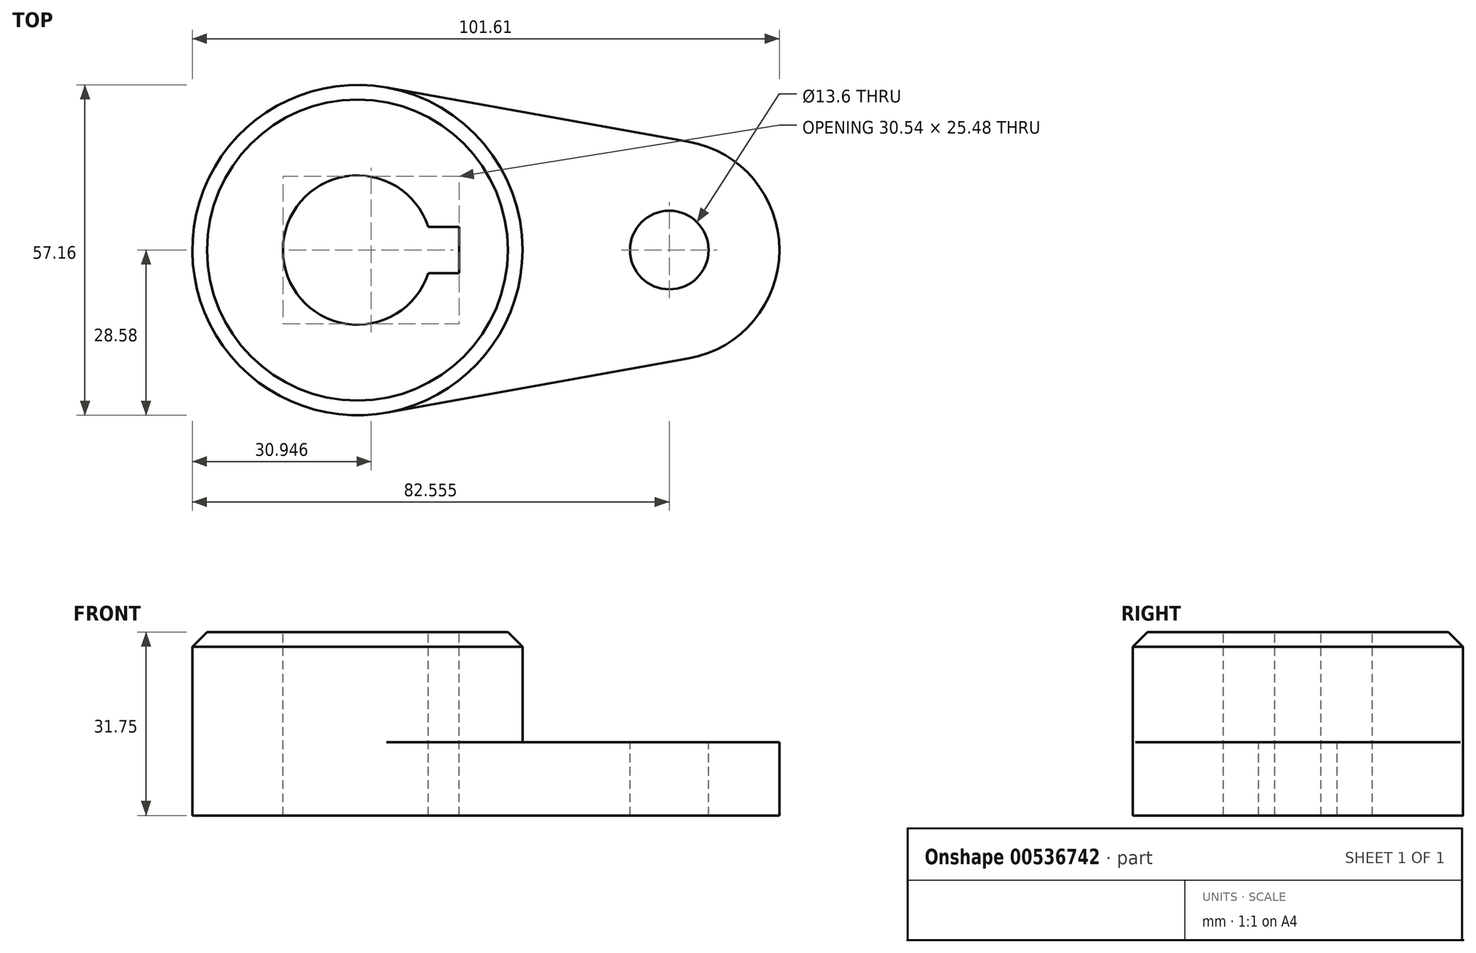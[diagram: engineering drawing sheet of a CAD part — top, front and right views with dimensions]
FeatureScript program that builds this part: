
annotation { "Feature Type Name" : "Feature", "Feature Type Description" : "" }
export const myFeature = defineFeature(function(context is Context, id is Id, definition is map)
    precondition{}
    {
        {
            var Q0;
            Q0=qCreatedBy(makeId("Top.planeOp"),FACE);
            var sketch = newSketch(context, id + "F0", { "sketchPlane" : qUnion([Q0])});
            skCircle(sketch, "E0", {"center": v(0, 0) * mm, "radius": 28.58 * mm});
            skArc(sketch, "E1", {"start": v(57.34, -18.75) * mm, "mid": v(73.03, 0) * mm, "end": v(57.34, 18.75) * mm});
            skLineSegment(sketch, "E2", {"start": v(57.34, 18.75) * mm, "end": v(5.04, 28.13) * mm});
            skLineSegment(sketch, "E3", {"start": v(5.04, -28.13) * mm, "end": v(57.34, -18.75) * mm});
            skSolve(sketch);
        }
        {
            var Q0;
            Q0 = qSketchRegion(id + "F0", true);
            extrude(context, id + "F1", {"entities" : qUnion([Q0]), "depth" : 12.7 * mm, "offsetDistance" : 25.4 * mm});
        }
        {
            var Q0;
            {var subQ0=sQuery(id+"F0.wireOp",EDGE,"E0");var subQ1=makeQuery(id+"F0.imprint","INTERSECT",VERTEX,{"derivedFrom":[subQ0,sQuery(id+"F0.wireOp",EDGE,"E2")]});Q0=makeQuery(id+"F0.imprint","IMPRINT",FACE,{"disambiguationData":[TD([[makeQuery(id+"F0.imprint","IMPRINT",EDGE,{"disambiguationData":[TD([[subQ1,-1.0]])],"derivedFrom":subQ0}),1.0]])]});}
            extrude(context, id + "F2", {"entities" : qUnion([Q0]), "operationType" : NewBodyOperationType.ADD, "depth" : 31.75 * mm, "offsetDistance" : 25.4 * mm});
        }
        {
            var Q0;
            Q0=makeQuery(id+"F1.opExtrude","CAP_FACE",FACE,{"disambiguationData":[OSD([sQuery(id+"F0.wireOp",EDGE,"E0"),sQuery(id+"F0.wireOp",EDGE,"E1"),sQuery(id+"F0.wireOp",EDGE,"E2"),sQuery(id+"F0.wireOp",EDGE,"E3")])],"isStart":false});
            var sketch = newSketch(context, id + "F3", { "sketchPlane" : qUnion([Q0])});
            skCircle(sketch, "E4", {"center": v(53.98, 0) * mm, "radius": 6.8 * mm});
            skSolve(sketch);
        }
        {
            var Q0;
            Q0 = qSketchRegion(id + "F3", true);
            extrude(context, id + "F4", {"entities" : qUnion([Q0]), "operationType" : NewBodyOperationType.REMOVE, "oppositeDirection" : true, "depth" : 25.4 * mm, "offsetDistance" : 25.4 * mm});
        }
        {
            var Q0;
            Q0=makeQuery(id+"F2.opExtrude","CAP_FACE",FACE,{"disambiguationData":[OSD([sQuery(id+"F0.wireOp",EDGE,"E0")])],"isStart":false});
            chamfer(context, id + "F5", {"entities" : qUnion([Q0]), "width" : 2.54 * mm, "tangentPropagation" : true});
        }
        {
            var Q0;
            Q0=makeQuery(id+"F2.opExtrude","CAP_FACE",FACE,{"disambiguationData":[OSD([sQuery(id+"F0.wireOp",EDGE,"E0")])],"isStart":false});
            var sketch = newSketch(context, id + "F6", { "sketchPlane" : qUnion([Q0])});
            skArc(sketch, "E5", {"start": v(12.26, 4.02) * mm, "mid": v(-12.9, 0) * mm, "end": v(12.26, -4.02) * mm});
            skLineSegment(sketch, "E6.bottom", {"start": v(17.64, -4.02) * mm, "end": v(12.26, -4.02) * mm});
            skLineSegment(sketch, "E6.top", {"start": v(17.64, 4.02) * mm, "end": v(12.26, 4.02) * mm});
            skLineSegment(sketch, "E6.left", {"start": v(17.64, -4.02) * mm, "end": v(17.64, 4.02) * mm});
            skSolve(sketch);
        }
        {
            var Q0;
            Q0=makeQuery(id+"F6.imprint","IMPRINT",FACE,{"disambiguationData":[TD([[makeQuery(id+"F6.imprint","IMPRINT",EDGE,{"derivedFrom":sQuery(id+"F6.wireOp",EDGE,"E5")}),1.0]])]});
            extrude(context, id + "F7", {"entities" : qUnion([Q0]), "operationType" : NewBodyOperationType.REMOVE, "endBound" : BoundingType.THROUGH_ALL, "oppositeDirection" : true, "depth" : 25.4 * mm, "offsetDistance" : 25.4 * mm});
        }
    });
